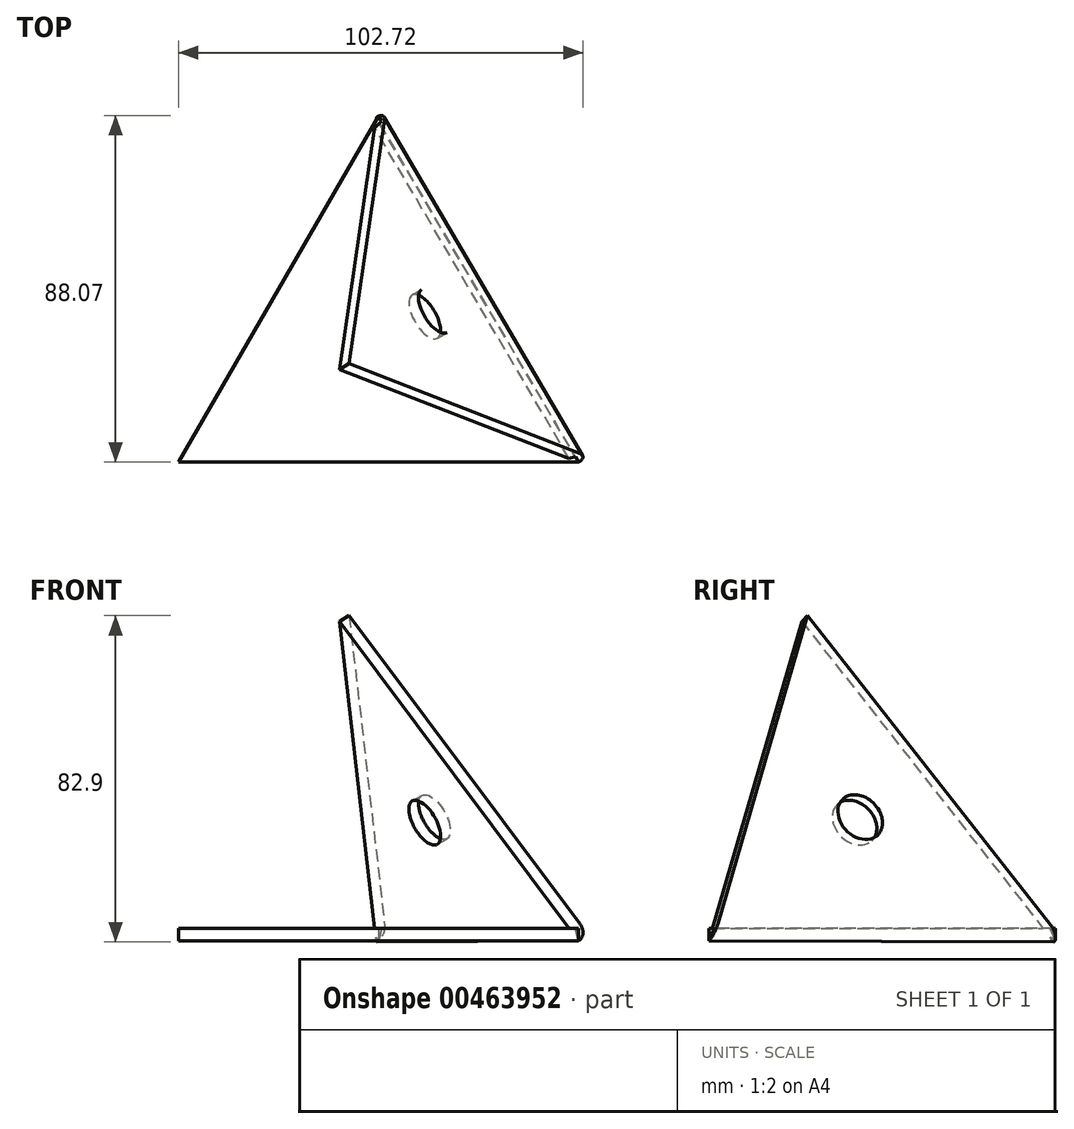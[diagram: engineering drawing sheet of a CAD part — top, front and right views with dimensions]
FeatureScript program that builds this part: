
annotation { "Feature Type Name" : "Feature", "Feature Type Description" : "" }
export const myFeature = defineFeature(function(context is Context, id is Id, definition is map)
    precondition{}
    {
        {
            var Q0;
            Q0=qCreatedBy(makeId("Top.planeOp"),FACE);
            var sketch = newSketch(context, id + "F0", { "sketchPlane" : qUnion([Q0])});
            skLineSegment(sketch, "E0", {"start": v(0, 87.99) * mm, "end": v(-50.8, 0) * mm});
            skLineSegment(sketch, "E1", {"start": v(-50.8, 0) * mm, "end": v(50.8, 0) * mm});
            skLineSegment(sketch, "E2", {"start": v(50.8, 0) * mm, "end": v(0, 87.99) * mm});
            skSolve(sketch);
        }
        {
            var Q0;
            Q0=makeQuery(id+"F0.imprint","IMPRINT",FACE,{"disambiguationData":[TD([[makeQuery(id+"F0.imprint","IMPRINT",EDGE,{"derivedFrom":sQuery(id+"F0.wireOp",EDGE,"E0")}),1.0]])]});
            extrude(context, id + "F1", {"entities" : qUnion([Q0]), "depth" : 3.17 * mm});
        }
        {
            var Q0;
            Q0=qCreatedBy(makeId("Front.planeOp"),FACE);
            var sketch = newSketch(context, id + "F2", { "sketchPlane" : qUnion([Q0])});
            skLineSegment(sketch, "E3", {"start": v(-50.8, 0) * mm, "end": v(0, 87.99) * mm});
            skLineSegment(sketch, "E4", {"start": v(0, 87.99) * mm, "end": v(50.8, 0) * mm});
            skLineSegment(sketch, "E5", {"start": v(-50.8, 0) * mm, "end": v(50.8, 0) * mm});
            skSolve(sketch);
        }
        {
            var Q0;
            Q0=qCreatedBy(makeId("Front.planeOp"),FACE);
            var Q1;
            Q1=sQuery(id+"F2.wireOp",EDGE,"E4");
            cPlane(context, id + "F3", {"entities" : qUnion([Q0, Q1]), "cplaneType" : CPlaneType.LINE_ANGLE, "offset" : 25.4 * mm, "angle" : 63 * degree, "width" : 152.4 * mm, "height" : 152.4 * mm});
        }
        {
            var Q0;
            Q0=qCreatedBy(id+"F3.planeOp",FACE);
            var sketch = newSketch(context, id + "F4", { "sketchPlane" : qUnion([Q0])});
            skLineSegment(sketch, "E6", {"start": v(-19.98, -25.4) * mm, "end": v(6.5, 75.25) * mm});
            skLineSegment(sketch, "E7", {"start": v(6.5, 75.25) * mm, "end": v(78.4, 0) * mm});
            skLineSegment(sketch, "E8", {"start": v(-19.98, -25.4) * mm, "end": v(78.4, 0) * mm});
            skSolve(sketch);
        }
        {
            var Q0;
            Q0=qSketchRegion(id+"F4",true);
            extrude(context, id + "F5", {"entities" : qUnion([Q0]), "operationType" : NewBodyOperationType.ADD, "depth" : 3.17 * mm});
        }
        {
            var Q0;
            Q0=makeQuery(id+"F5.opExtrude","CAP_EDGE",EDGE,{"disambiguationData":[OSD([sQuery(id+"F4.wireOp",EDGE,"E8")])],"isStart":false});
            fillet(context, id + "F6", {"entities" : qUnion([Q0]), "radius" : 3.17 * mm, "tangentPropagation" : true, "allowEdgeOverflow" : false});
        }
        {
            var Q0;
            Q0=makeQuery(id+"F5.opExtrude","CAP_FACE",FACE,{"disambiguationData":[OSD([sQuery(id+"F4.wireOp",EDGE,"E6"),sQuery(id+"F4.wireOp",EDGE,"E7"),sQuery(id+"F4.wireOp",EDGE,"E8")])],"isStart":false});
            var sketch = newSketch(context, id + "F7", { "sketchPlane" : qUnion([Q0])});
            skCircle(sketch, "E9", {"center": v(21.55, 20.11) * mm, "radius": 6.35 * mm});
            skLineSegment(sketch, "E10", {"start": v(6.5, 75.25) * mm, "end": v(30.41, -12.39) * mm});
            skSolve(sketch);
        }
        {
            var Q0;
            {var subQ0=sQuery(id+"F7.wireOp",EDGE,"E10");var subQ1=sQuery(id+"F7.wireOp",EDGE,"E9");var subQ2=makeQuery(id+"F7.imprint","INTERSECT",VERTEX,{"disambiguationData":[OD(0.0)],"derivedFrom":[subQ1,subQ0]});Q0=makeQuery(id+"F7.imprint","IMPRINT",FACE,{"disambiguationData":[TD([[makeQuery(id+"F7.imprint","IMPRINT",EDGE,{"disambiguationData":[TD([[subQ2,1.0]])],"derivedFrom":subQ1}),1.0]])]});}
            var Q1;
            {var subQ0=sQuery(id+"F7.wireOp",EDGE,"E10");var subQ1=sQuery(id+"F7.wireOp",EDGE,"E9");var subQ2=makeQuery(id+"F7.imprint","INTERSECT",VERTEX,{"disambiguationData":[OD(0.0)],"derivedFrom":[subQ1,subQ0]});Q1=makeQuery(id+"F7.imprint","IMPRINT",FACE,{"disambiguationData":[TD([[makeQuery(id+"F7.imprint","IMPRINT",EDGE,{"disambiguationData":[TD([[subQ2,-1.0]])],"derivedFrom":subQ1}),1.0]])]});}
            extrude(context, id + "F8", {"entities" : qUnion([Q0, Q1]), "operationType" : NewBodyOperationType.REMOVE, "endBound" : BoundingType.UP_TO_NEXT, "oppositeDirection" : true, "depth" : 25.4 * mm});
        }
    });
